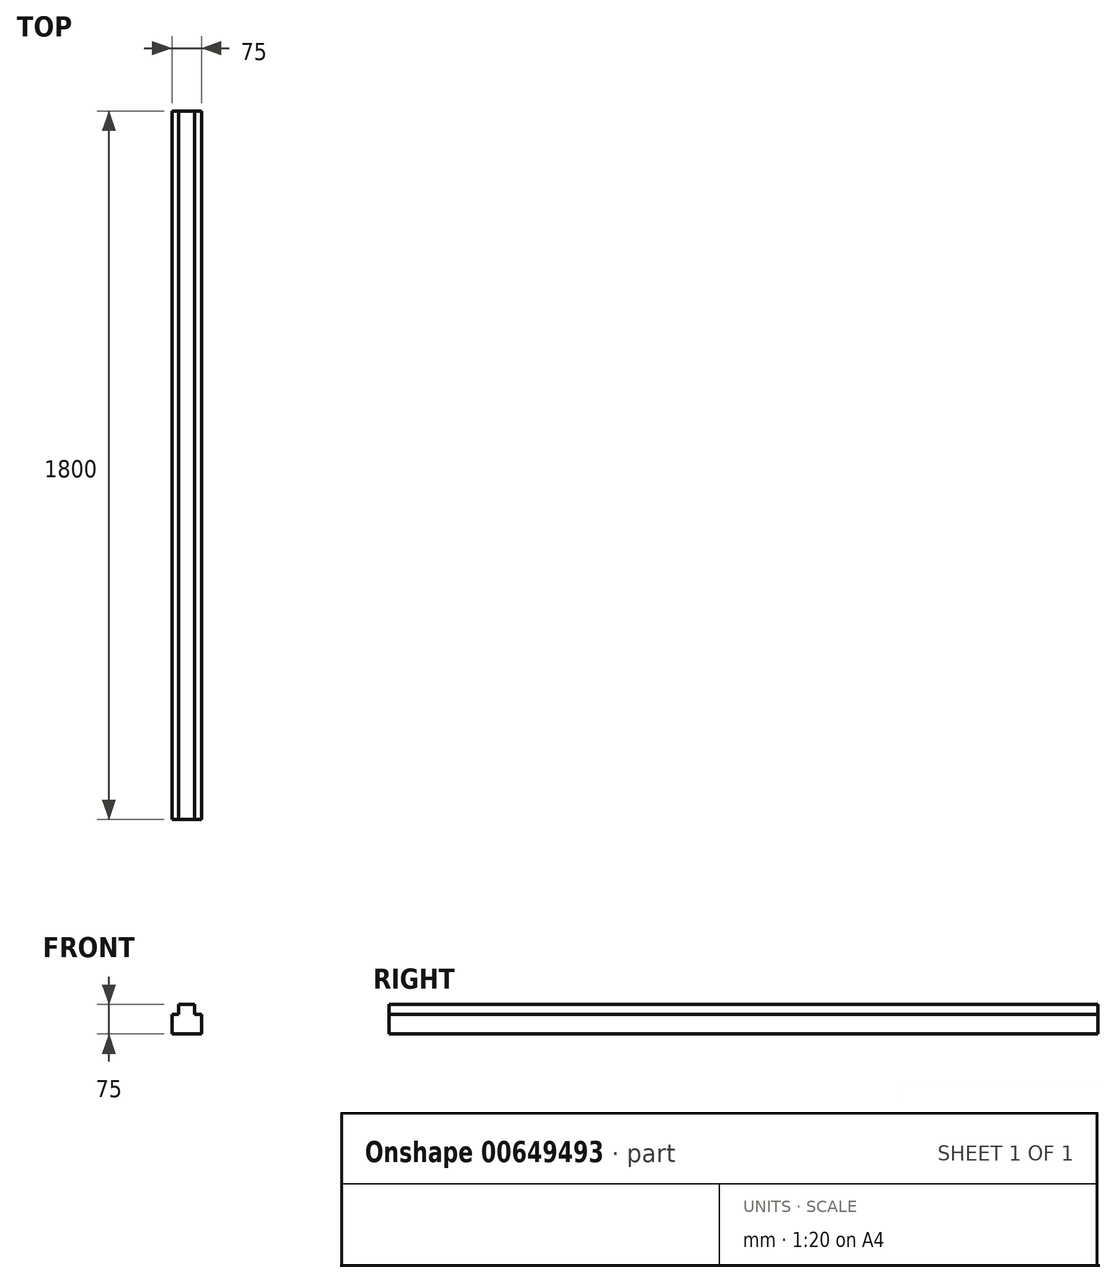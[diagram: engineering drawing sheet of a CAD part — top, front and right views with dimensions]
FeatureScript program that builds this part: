
annotation { "Feature Type Name" : "Feature", "Feature Type Description" : "" }
export const myFeature = defineFeature(function(context is Context, id is Id, definition is map)
    precondition{}
    {
        {
            var Q0;
            Q0=qCreatedBy(makeId("Front.planeOp"),FACE);
            var sketch = newSketch(context, id + "F0", { "sketchPlane" : qUnion([Q0])});
            skLineSegment(sketch, "E0", {"start": v(0, 0) * mm, "end": v(37.5, 0) * mm});
            skLineSegment(sketch, "E1", {"start": v(37.5, 0) * mm, "end": v(37.5, 50) * mm});
            skLineSegment(sketch, "E2", {"start": v(37.5, 50) * mm, "end": v(20, 50) * mm});
            skLineSegment(sketch, "E3", {"start": v(20, 50) * mm, "end": v(20, 75) * mm});
            skLineSegment(sketch, "E4", {"start": v(20, 75) * mm, "end": v(0, 75) * mm});
            skLineSegment(sketch, "E5.MirrorCS", {"start": v(-20, 75) * mm, "end": v(0, 75) * mm});
            skLineSegment(sketch, "E6.MirrorCS", {"start": v(0, 0) * mm, "end": v(-37.5, 0) * mm});
            skLineSegment(sketch, "E7.MirrorCS", {"start": v(-37.5, 0) * mm, "end": v(-37.5, 50) * mm});
            skLineSegment(sketch, "E8.MirrorCS", {"start": v(-20, 50) * mm, "end": v(-20, 75) * mm});
            skLineSegment(sketch, "E9.MirrorCS", {"start": v(-37.5, 50) * mm, "end": v(-20, 50) * mm});
            skSolve(sketch);
        }
        {
            var Q0;
            Q0=makeQuery(id+"F0.imprint","IMPRINT",FACE,{"disambiguationData":[TD([[makeQuery(id+"F0.imprint","IMPRINT",EDGE,{"derivedFrom":sQuery(id+"F0.wireOp",EDGE,"E0")}),1.0]])]});
            extrude(context, id + "F1", {"entities" : qUnion([Q0]), "depth" : 1800 * mm, "offsetDistance" : 25 * mm});
        }
    });
